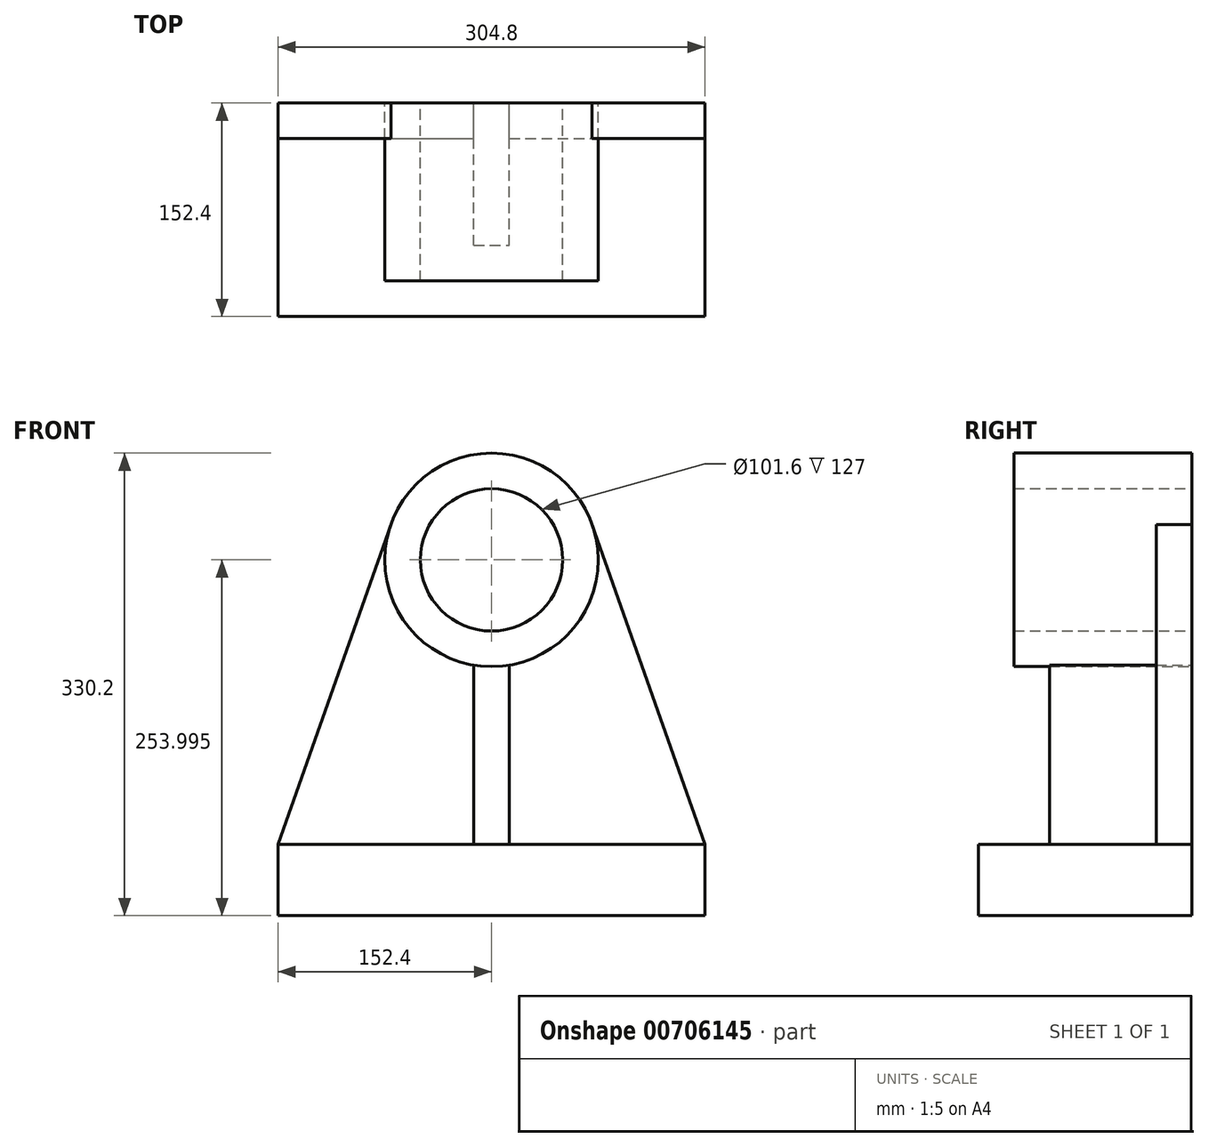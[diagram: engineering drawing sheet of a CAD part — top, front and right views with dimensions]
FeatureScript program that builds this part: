
annotation { "Feature Type Name" : "Feature", "Feature Type Description" : "" }
export const myFeature = defineFeature(function(context is Context, id is Id, definition is map)
    precondition{}
    {
        {
            var Q0;
            Q0=qCreatedBy(makeId("Front.planeOp"),FACE);
            var sketch = newSketch(context, id + "F0", { "sketchPlane" : qUnion([Q0])});
            skLineSegment(sketch, "E0", {"start": v(-152.4, -51.2) * mm, "end": v(152.4, -51.2) * mm});
            skLineSegment(sketch, "E1", {"start": v(152.4, -51.2) * mm, "end": v(152.4, -102) * mm});
            skLineSegment(sketch, "E2", {"start": v(152.4, -102) * mm, "end": v(-152.4, -102) * mm});
            skLineSegment(sketch, "E3", {"start": v(-152.4, -102) * mm, "end": v(-152.4, -51.2) * mm});
            skCircle(sketch, "E4", {"center": v(0, 152) * mm, "radius": 76.2 * mm});
            skCircle(sketch, "E5", {"center": v(0, 152) * mm, "radius": 50.8 * mm});
            skLineSegment(sketch, "E6", {"start": v(-152.4, -51.2) * mm, "end": v(-71.87, 177.32) * mm});
            skLineSegment(sketch, "E7", {"start": v(152.4, -51.2) * mm, "end": v(71.87, 177.32) * mm});
            skLineSegment(sketch, "E8", {"start": v(0, 228.2) * mm, "end": v(0, -51.2) * mm, "construction": true});
            skPoint(sketch, "E8.endSnap0", {"position": v(0, -51.2) * mm});
            skLineSegment(sketch, "E9", {"start": v(-12.7, 76.86) * mm, "end": v(-12.7, -51.2) * mm});
            skLineSegment(sketch, "E10", {"start": v(12.7, 76.86) * mm, "end": v(12.7, -51.2) * mm});
            skSolve(sketch);
        }
        {
            var Q0;
            Q0=makeQuery(id+"F0.imprint","IMPRINT",FACE,{"disambiguationData":[TD([[makeQuery(id+"F0.imprint","IMPRINT",EDGE,{"derivedFrom":sQuery(id+"F0.wireOp",EDGE,"E5")}),-1.0]])]});
            extrude(context, id + "F1", {"entities" : qUnion([Q0]), "depth" : 127 * mm, "offsetDistance" : 25.4 * mm});
        }
        {
            var Q0;
            {var subQ0=sQuery(id+"F0.wireOp",EDGE,"E1");Q0=makeQuery(id+"F0.imprint","IMPRINT",FACE,{"disambiguationData":[TD([[makeQuery(id+"F0.imprint","IMPRINT",EDGE,{"derivedFrom":subQ0}),-1.0]])]});}
            extrude(context, id + "F2", {"entities" : qUnion([Q0]), "depth" : 152.4 * mm, "offsetDistance" : 25.4 * mm});
        }
        {
            var Q0;
            {var subQ0=sQuery(id+"F0.wireOp",EDGE,"E9");Q0=makeQuery(id+"F0.imprint","IMPRINT",FACE,{"disambiguationData":[TD([[makeQuery(id+"F0.imprint","IMPRINT",EDGE,{"derivedFrom":subQ0}),1.0]])]});}
            extrude(context, id + "F3", {"entities" : qUnion([Q0]), "depth" : 101.6 * mm, "offsetDistance" : 25.4 * mm});
        }
        {
            var Q0;
            {var subQ0=sQuery(id+"F0.wireOp",EDGE,"E6");Q0=makeQuery(id+"F0.imprint","IMPRINT",FACE,{"disambiguationData":[TD([[makeQuery(id+"F0.imprint","IMPRINT",EDGE,{"derivedFrom":subQ0}),-1.0]])]});}
            var Q1;
            {var subQ0=sQuery(id+"F0.wireOp",EDGE,"E7");Q1=makeQuery(id+"F0.imprint","IMPRINT",FACE,{"disambiguationData":[TD([[makeQuery(id+"F0.imprint","IMPRINT",EDGE,{"derivedFrom":subQ0}),1.0]])]});}
            extrude(context, id + "F4", {"entities" : qUnion([Q0, Q1]), "depth" : 25.4 * mm, "offsetDistance" : 25.4 * mm});
        }
    });
